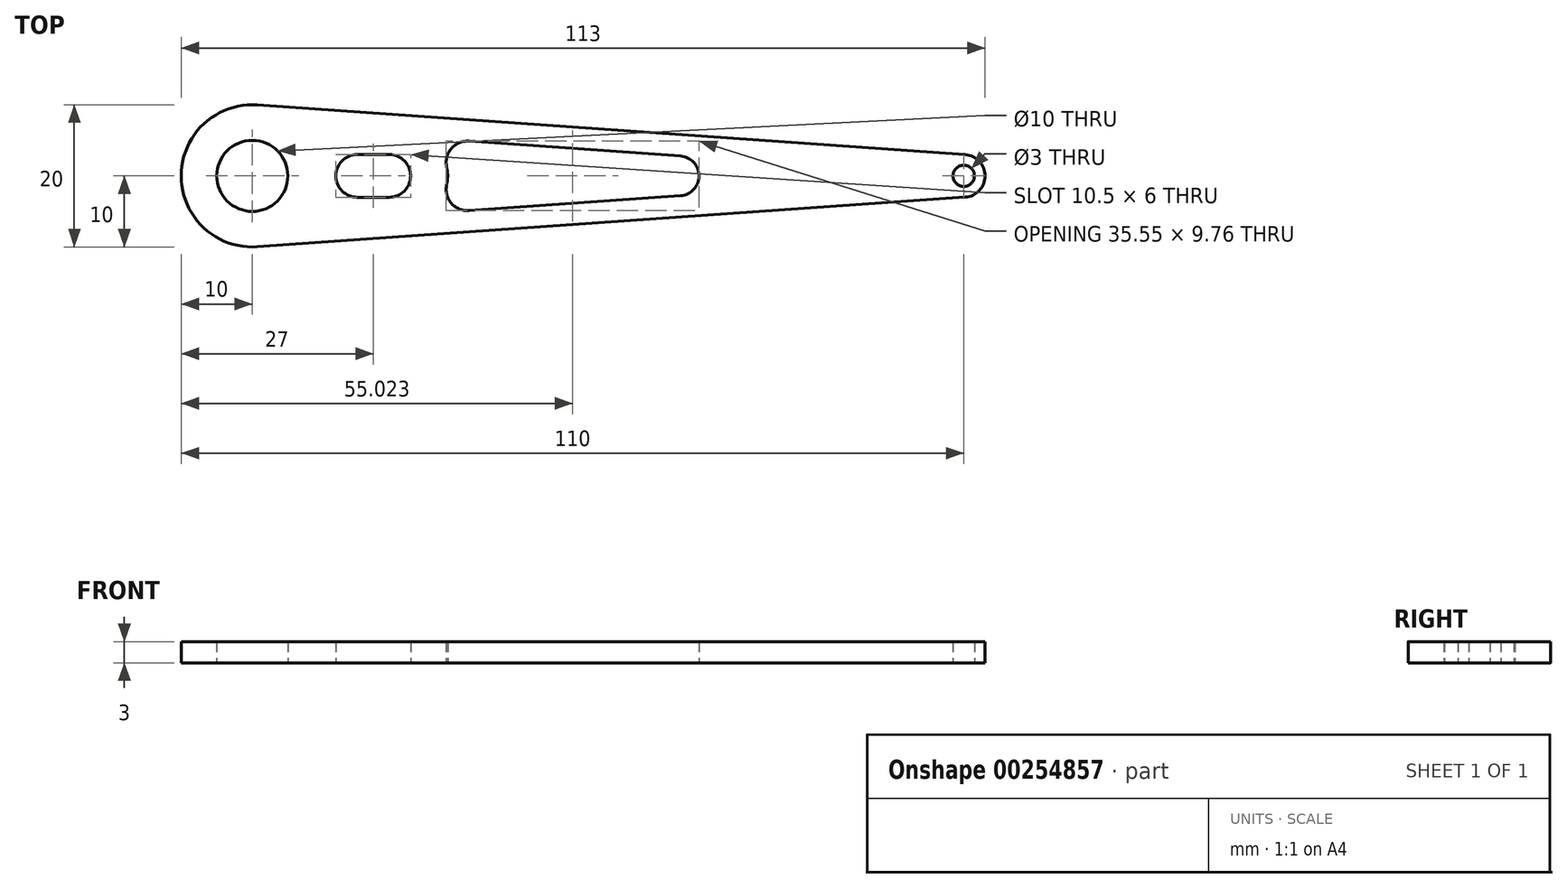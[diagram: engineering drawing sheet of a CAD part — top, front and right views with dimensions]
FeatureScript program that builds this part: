
annotation { "Feature Type Name" : "Feature", "Feature Type Description" : "" }
export const myFeature = defineFeature(function(context is Context, id is Id, definition is map)
    precondition{}
    {
        {
            var Q0;
            Q0=qCreatedBy(makeId("Top.planeOp"),FACE);
            var sketch = newSketch(context, id + "F0", { "sketchPlane" : qUnion([Q0])});
            skArc(sketch, "E0", {"start": v(-49.3, 9.98) * mm, "mid": v(-60, 0) * mm, "end": v(-49.3, -9.98) * mm});
            skArc(sketch, "E1", {"start": v(50.2, -3) * mm, "mid": v(53, 0) * mm, "end": v(50.2, 3) * mm});
            skLineSegment(sketch, "E2", {"start": v(-49.3, 9.98) * mm, "end": v(50.21, 3) * mm});
            skLineSegment(sketch, "E3", {"start": v(-49.3, -9.98) * mm, "end": v(50.21, -3) * mm});
            skCircle(sketch, "E4", {"center": v(50, 0) * mm, "radius": 1.5 * mm});
            skArc(sketch, "E5", {"start": v(-22.68, -1.22) * mm, "mid": v(-22.54, 0) * mm, "end": v(-22.68, 1.22) * mm});
            skArc(sketch, "E6", {"start": v(10.2, -2.8) * mm, "mid": v(12.8, 0) * mm, "end": v(10.2, 2.8) * mm});
            skLineSegment(sketch, "E7", {"start": v(-19.54, 4.88) * mm, "end": v(10.2, 2.8) * mm});
            skLineSegment(sketch, "E8", {"start": v(-19.54, -4.88) * mm, "end": v(10.2, -2.8) * mm});
            skPoint(sketch, "E9.visualSharp", {"position": v(-27.62, 5.45) * mm});
            skArc(sketch, "E9.filletArc", {"start": v(-19.54, 4.88) * mm, "mid": v(-22.03, 3.84) * mm, "end": v(-22.68, 1.22) * mm});
            skPoint(sketch, "E10.visualSharp", {"position": v(-27.62, -5.45) * mm});
            skArc(sketch, "E10.filletArc", {"start": v(-22.68, -1.22) * mm, "mid": v(-22.03, -3.84) * mm, "end": v(-19.54, -4.88) * mm});
            skCircle(sketch, "E11", {"center": v(-50, 0) * mm, "radius": 5 * mm});
            skArc(sketch, "E12", {"start": v(-35.25, 3) * mm, "mid": v(-38.25, 0) * mm, "end": v(-35.25, -3) * mm});
            skLineSegment(sketch, "E13", {"start": v(-35.25, -3) * mm, "end": v(-30.75, -3) * mm});
            skArc(sketch, "E14", {"start": v(-30.75, -3) * mm, "mid": v(-27.75, 0) * mm, "end": v(-30.75, 3) * mm});
            skLineSegment(sketch, "E15", {"start": v(-35.25, 3) * mm, "end": v(-30.75, 3) * mm});
            skSolve(sketch);
        }
        {
            var Q0;
            Q0 = qSketchRegion(id + "F0", true);
            extrude(context, id + "F1", {"entities" : qUnion([Q0]), "depth" : 3 * mm, "symmetric" : true});
        }
    });
